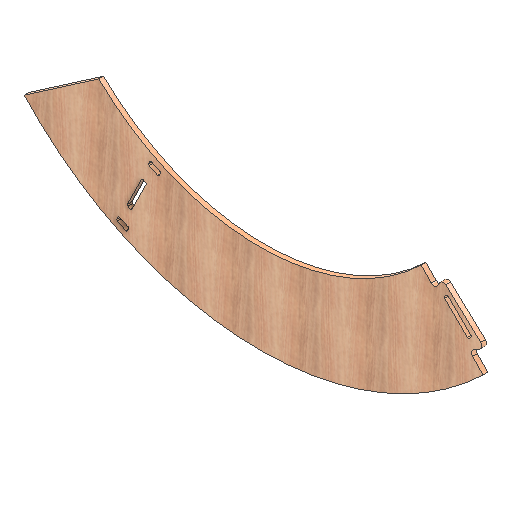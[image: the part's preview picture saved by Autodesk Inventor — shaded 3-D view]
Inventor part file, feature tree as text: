
AUTODESK INVENTOR PART (.ipt)
format: ipt  version: 2021 (Build 250183000, 183)  size: 257,024 bytes
history: native  units: mm
features: other x2, extrude x2, hole x1
ambient origin geometry x8: Origin, YZ Plane, XZ Plane, XY Plane, X Axis, Y Axis, Z Axis, Center Point
bodies: Body1 (feature_tree)
feature tree (5):
  other  "CONTOURS"
  hole  "HOLES"  [1 undecoded]
  other  "LETTERS"
  extrude  "Extrusion3"  Depth=880.606242mm
  extrude  "Extrusion4"  Depth=0.011356mm
note: 1 required parameter value undecoded (feature->parameter linkage not recoverable at this tier; creation-order binding heuristic only, values carry confidence <= 0.55)
